# Revit family: RN 55033 Optipress-Therm-Übergang
name_source: partatom
category: Rohrformteile
units: mm (PartAtom-declared; Revit-internal decimal feet)

## family parameters
Arbeitsebenenbasiert = Nein
Beim Laden mit Abzugskörper schneiden = Nein
Bemaßung runder Anschluss = Durchmesser verwenden
Gemeinsam genutzt = Nein
Immer vertikal = Ja
Teiletyp = Verbindung

## types (22) — shared parameters
1.010.00.2 Blattnummer der Richtlinie = 29
1.010.00.3 Ausgabedatum (Monat) der Richtlinie = 201308
1.010.00.4 Herstellername = R. Nussbaum AG
1.010.00.5 Revisionsdatum der Datei = 20190521
1.010.00.6 Webadresse des Herstellers = http://www.nussbaum.ch
1.100.00.4 Produktbezeichnung = Versorgung
1.110.00.2 Index = 1
1.110.00.4 Produktbezeichnung = Optipress-Therm
1.960/3L.00.8 Link (URL) = https://www.nussbaum.ch
29.700.00.4 Produktname = Optipress-Therm-Übergang, mit Innengewinde
29.700.00.5 Produktkennung = 2
29.700.00.6 Querschnittsform = 1
29.700.00.7 Nennweitensystem = DN
29.700.00.8 Nenndrucksystem = PN
29.710.02.4 Nenndruck = 16
29.710.02.5 max. zul. Überdruck [hPa] = 1600
29.710.02.7 max. zul. Dauer-Betriebsdruck [hPa] = 1600
29.710.02.9 max. zul. Dauer-Betriebstemperatur [°C] = 95
Connector Visibility = Nein
EnclosingSpace Visibility = Nein

## per-type parameters (varying)
- DN=60x50: 1.800.00.3 TGA-Nummer=01900100000000000000000000000000000000000000000020000000000000000022; 1.800.00.4 Kommentarfeld=55033.70, Optipress-Therm-Übergang, mit Innengewinde, DN=60x50, L=88, Rp=2; 1.810.00.3 Hersteller-Bestellnummer=55033.7; 1.810.00.4 DATANORM-Nummer=55033.70; 1.810.00.5 StLB-Nummer=255.644; 1.810.00.6 GTIN-Nummer=7612945685605; 29.710.02.10 Formstück-Gewicht [kg]=0.403; 29.710.02.3 Benennung=Optipress-Therm-Übergang, mit Innengewinde, DN=60x50, L=88, Rp=2; CONNECTOR0_DIAMETER_dX_0r=60 mm; CONNECTOR0_dX_01=43 mm  [stored 0.141076 ft]; CONNECTOR0_ref_dX=43 mm  [stored 0.141076 ft]; CONNECTOR1_DIAMETER_dX_0r=50 mm; CONNECTOR1_dX_00=89 mm; CONNECTOR1_dX_01=113 mm; CONNECTOR1_ref_dX=113 mm; Hersteller=R. Nussbaum AG; Modell=55033.7; R. Nussbaum AG 55033.21 de Visibility=Nein; R. Nussbaum AG 55033.22 de Visibility=Nein; R. Nussbaum AG 55033.23 de Visibility=Nein; R. Nussbaum AG 55033.24 de Visibility=Nein; R. Nussbaum AG 55033.25 de Visibility=Nein; R. Nussbaum AG 55033.26 de Visibility=Nein; R. Nussbaum AG 55033.27 de Visibility=Nein; R. Nussbaum AG 55033.28 de Visibility=Nein; R. Nussbaum AG 55033.29 de Visibility=Nein; R. Nussbaum AG 55033.30 de Visibility=Nein; R. Nussbaum AG 55033.31 de Visibility=Nein; R. Nussbaum AG 55033.32 de Visibility=Nein; R. Nussbaum AG 55033.33 de Visibility=Nein; R. Nussbaum AG 55033.34 de Visibility=Nein; R. Nussbaum AG 55033.35 de Visibility=Nein; R. Nussbaum AG 55033.36 de Visibility=Nein; R. Nussbaum AG 55033.37 de Visibility=Nein; R. Nussbaum AG 55033.70 de Visibility=Ja; R. Nussbaum AG 55033.71 de Visibility=Nein; R. Nussbaum AG 55033.72 de Visibility=Nein; R. Nussbaum AG 55033.73 de Visibility=Nein; R. Nussbaum AG 55033.74 de Visibility=Nein; Typenkommentare=Optipress-Therm-Übergang DN=60x50
- DN=25x15: 1.800.00.3 TGA-Nummer=01900100000000000000000000000000000000000000000020000000000000000021; 1.800.00.4 Kommentarfeld=55033.30, Optipress-Therm-Übergang, mit Innengewinde, DN=25x15, L=38, Rp=½; 1.810.00.3 Hersteller-Bestellnummer=55033.3; 1.810.00.4 DATANORM-Nummer=55033.30; 1.810.00.5 StLB-Nummer=255.635; 1.810.00.6 GTIN-Nummer=7612945708946; 29.710.02.10 Formstück-Gewicht [kg]=0.115; 29.710.02.3 Benennung=Optipress-Therm-Übergang, mit Innengewinde, DN=25x15, L=38, Rp=½; CONNECTOR0_DIAMETER_dX_0r=25 mm  [stored 0.082021 ft]; CONNECTOR0_dX_01=24 mm; CONNECTOR0_ref_dX=24 mm; CONNECTOR1_DIAMETER_dX_0r=15 mm  [stored 0.0492126 ft]; CONNECTOR1_dX_00=24 mm; CONNECTOR1_dX_01=38 mm  [stored 0.124672 ft]; CONNECTOR1_ref_dX=24 mm; Hersteller=R. Nussbaum AG; Modell=55033.3; R. Nussbaum AG 55033.21 de Visibility=Nein; R. Nussbaum AG 55033.22 de Visibility=Nein; R. Nussbaum AG 55033.23 de Visibility=Nein; R. Nussbaum AG 55033.24 de Visibility=Nein; R. Nussbaum AG 55033.25 de Visibility=Nein; R. Nussbaum AG 55033.26 de Visibility=Nein; R. Nussbaum AG 55033.27 de Visibility=Nein; R. Nussbaum AG 55033.28 de Visibility=Nein; R. Nussbaum AG 55033.29 de Visibility=Nein; R. Nussbaum AG 55033.30 de Visibility=Ja; R. Nussbaum AG 55033.31 de Visibility=Nein; R. Nussbaum AG 55033.32 de Visibility=Nein; R. Nussbaum AG 55033.33 de Visibility=Nein; R. Nussbaum AG 55033.34 de Visibility=Nein; R. Nussbaum AG 55033.35 de Visibility=Nein; R. Nussbaum AG 55033.36 de Visibility=Nein; R. Nussbaum AG 55033.37 de Visibility=Nein; R. Nussbaum AG 55033.70 de Visibility=Nein; R. Nussbaum AG 55033.71 de Visibility=Nein; R. Nussbaum AG 55033.72 de Visibility=Nein; R. Nussbaum AG 55033.73 de Visibility=Nein; R. Nussbaum AG 55033.74 de Visibility=Nein; Typenkommentare=Optipress-Therm-Übergang DN=25x15
- DN=100: 1.800.00.3 TGA-Nummer=01900100000000000000000000000000000000000000000020000000000000000020; 1.800.00.4 Kommentarfeld=55033.74, Optipress-Therm-Übergang, mit Innengewinde, DN=100, L=135, Rp=4; 1.810.00.3 Hersteller-Bestellnummer=55033.74; 1.810.00.4 DATANORM-Nummer=55033.74; 1.810.00.5 StLB-Nummer=255.643; 1.810.00.6 GTIN-Nummer=7612945699220; 29.710.02.10 Formstück-Gewicht [kg]=1.453; 29.710.02.3 Benennung=Optipress-Therm-Übergang, mit Innengewinde, DN=100, L=135, Rp=4; CONNECTOR0_DIAMETER_dX_0r=100 mm  [stored 0.328084 ft]; CONNECTOR0_dX_01=60 mm; CONNECTOR0_ref_dX=60 mm; CONNECTOR1_DIAMETER_dX_0r=100 mm  [stored 0.328084 ft]; CONNECTOR1_dX_00=98 mm; CONNECTOR1_dX_01=134 mm; CONNECTOR1_ref_dX=98 mm; Hersteller=R. Nussbaum AG; Modell=55033.74; R. Nussbaum AG 55033.21 de Visibility=Nein; R. Nussbaum AG 55033.22 de Visibility=Nein; R. Nussbaum AG 55033.23 de Visibility=Nein; R. Nussbaum AG 55033.24 de Visibility=Nein; R. Nussbaum AG 55033.25 de Visibility=Nein; R. Nussbaum AG 55033.26 de Visibility=Nein; R. Nussbaum AG 55033.27 de Visibility=Nein; R. Nussbaum AG 55033.28 de Visibility=Nein; R. Nussbaum AG 55033.29 de Visibility=Nein; R. Nussbaum AG 55033.30 de Visibility=Nein; R. Nussbaum AG 55033.31 de Visibility=Nein; R. Nussbaum AG 55033.32 de Visibility=Nein; R. Nussbaum AG 55033.33 de Visibility=Nein; R. Nussbaum AG 55033.34 de Visibility=Nein; R. Nussbaum AG 55033.35 de Visibility=Nein; R. Nussbaum AG 55033.36 de Visibility=Nein; R. Nussbaum AG 55033.37 de Visibility=Nein; R. Nussbaum AG 55033.70 de Visibility=Nein; R. Nussbaum AG 55033.71 de Visibility=Nein; R. Nussbaum AG 55033.72 de Visibility=Nein; R. Nussbaum AG 55033.73 de Visibility=Nein; R. Nussbaum AG 55033.74 de Visibility=Ja; Typenkommentare=Optipress-Therm-Übergang DN=100
- DN=80: 1.800.00.3 TGA-Nummer=01900100000000000000000000000000000000000000000020000000000000000019; 1.800.00.4 Kommentarfeld=55033.73, Optipress-Therm-Übergang, mit Innengewinde, DN=80, L=114, Rp=3; 1.810.00.3 Hersteller-Bestellnummer=55033.73; 1.810.00.4 DATANORM-Nummer=55033.73; 1.810.00.5 StLB-Nummer=255.642; 1.810.00.6 GTIN-Nummer=7612945699213; 29.710.02.10 Formstück-Gewicht [kg]=1.165; 29.710.02.3 Benennung=Optipress-Therm-Übergang, mit Innengewinde, DN=80, L=114, Rp=3; CONNECTOR0_DIAMETER_dX_0r=80 mm; CONNECTOR0_dX_01=50 mm; CONNECTOR0_ref_dX=50 mm; CONNECTOR1_DIAMETER_dX_0r=80 mm; CONNECTOR1_dX_00=84 mm; CONNECTOR1_dX_01=114 mm; CONNECTOR1_ref_dX=84 mm; Hersteller=R. Nussbaum AG; Modell=55033.73; R. Nussbaum AG 55033.21 de Visibility=Nein; R. Nussbaum AG 55033.22 de Visibility=Nein; R. Nussbaum AG 55033.23 de Visibility=Nein; R. Nussbaum AG 55033.24 de Visibility=Nein; R. Nussbaum AG 55033.25 de Visibility=Nein; R. Nussbaum AG 55033.26 de Visibility=Nein; R. Nussbaum AG 55033.27 de Visibility=Nein; R. Nussbaum AG 55033.28 de Visibility=Nein; R. Nussbaum AG 55033.29 de Visibility=Nein; R. Nussbaum AG 55033.30 de Visibility=Nein; R. Nussbaum AG 55033.31 de Visibility=Nein; R. Nussbaum AG 55033.32 de Visibility=Nein; R. Nussbaum AG 55033.33 de Visibility=Nein; R. Nussbaum AG 55033.34 de Visibility=Nein; R. Nussbaum AG 55033.35 de Visibility=Nein; R. Nussbaum AG 55033.36 de Visibility=Nein; R. Nussbaum AG 55033.37 de Visibility=Nein; R. Nussbaum AG 55033.70 de Visibility=Nein; R. Nussbaum AG 55033.71 de Visibility=Nein; R. Nussbaum AG 55033.72 de Visibility=Nein; R. Nussbaum AG 55033.73 de Visibility=Ja; R. Nussbaum AG 55033.74 de Visibility=Nein; Typenkommentare=Optipress-Therm-Übergang DN=80
- DN=65: 1.800.00.3 TGA-Nummer=01900100000000000000000000000000000000000000000020000000000000000018; 1.800.00.4 Kommentarfeld=55033.72, Optipress-Therm-Übergang, mit Innengewinde, DN=65, L=104, Rp=2½; 1.810.00.3 Hersteller-Bestellnummer=55033.72; 1.810.00.4 DATANORM-Nummer=55033.72; 1.810.00.5 StLB-Nummer=255.641; 1.810.00.6 GTIN-Nummer=7612945685629; 29.710.02.10 Formstück-Gewicht [kg]=0.67; 29.710.02.3 Benennung=Optipress-Therm-Übergang, mit Innengewinde, DN=65, L=104, Rp=2½; CONNECTOR0_DIAMETER_dX_0r=65 mm; CONNECTOR0_dX_01=50 mm; CONNECTOR0_ref_dX=50 mm; CONNECTOR1_DIAMETER_dX_0r=65 mm; CONNECTOR1_dX_00=78 mm; CONNECTOR1_dX_01=105 mm; CONNECTOR1_ref_dX=78 mm; Hersteller=R. Nussbaum AG; Modell=55033.72; R. Nussbaum AG 55033.21 de Visibility=Nein; R. Nussbaum AG 55033.22 de Visibility=Nein; R. Nussbaum AG 55033.23 de Visibility=Nein; R. Nussbaum AG 55033.24 de Visibility=Nein; R. Nussbaum AG 55033.25 de Visibility=Nein; R. Nussbaum AG 55033.26 de Visibility=Nein; R. Nussbaum AG 55033.27 de Visibility=Nein; R. Nussbaum AG 55033.28 de Visibility=Nein; R. Nussbaum AG 55033.29 de Visibility=Nein; R. Nussbaum AG 55033.30 de Visibility=Nein; R. Nussbaum AG 55033.31 de Visibility=Nein; R. Nussbaum AG 55033.32 de Visibility=Nein; R. Nussbaum AG 55033.33 de Visibility=Nein; R. Nussbaum AG 55033.34 de Visibility=Nein; R. Nussbaum AG 55033.35 de Visibility=Nein; R. Nussbaum AG 55033.36 de Visibility=Nein; R. Nussbaum AG 55033.37 de Visibility=Nein; R. Nussbaum AG 55033.70 de Visibility=Nein; R. Nussbaum AG 55033.71 de Visibility=Nein; R. Nussbaum AG 55033.72 de Visibility=Ja; R. Nussbaum AG 55033.73 de Visibility=Nein; R. Nussbaum AG 55033.74 de Visibility=Nein; Typenkommentare=Optipress-Therm-Übergang DN=65
- DN=60x65: 1.800.00.3 TGA-Nummer=01900100000000000000000000000000000000000000000020000000000000000017; 1.800.00.4 Kommentarfeld=55033.71, Optipress-Therm-Übergang, mit Innengewinde, DN=60x65, L=98, Rp=2½; 1.810.00.3 Hersteller-Bestellnummer=55033.71; 1.810.00.4 DATANORM-Nummer=55033.71; 1.810.00.5 StLB-Nummer=255.644; 1.810.00.6 GTIN-Nummer=7612945685612; 29.710.02.10 Formstück-Gewicht [kg]=0.649; 29.710.02.3 Benennung=Optipress-Therm-Übergang, mit Innengewinde, DN=60x65, L=98, Rp=2½; CONNECTOR0_DIAMETER_dX_0r=60 mm; CONNECTOR0_dX_01=43 mm  [stored 0.141076 ft]; CONNECTOR0_ref_dX=43 mm  [stored 0.141076 ft]; CONNECTOR1_DIAMETER_dX_0r=50 mm; CONNECTOR1_dX_00=99 mm; CONNECTOR1_dX_01=126 mm; CONNECTOR1_ref_dX=126 mm; Hersteller=R. Nussbaum AG; Modell=55033.71; R. Nussbaum AG 55033.21 de Visibility=Nein; R. Nussbaum AG 55033.22 de Visibility=Nein; R. Nussbaum AG 55033.23 de Visibility=Nein; R. Nussbaum AG 55033.24 de Visibility=Nein; R. Nussbaum AG 55033.25 de Visibility=Nein; R. Nussbaum AG 55033.26 de Visibility=Nein; R. Nussbaum AG 55033.27 de Visibility=Nein; R. Nussbaum AG 55033.28 de Visibility=Nein; R. Nussbaum AG 55033.29 de Visibility=Nein; R. Nussbaum AG 55033.30 de Visibility=Nein; R. Nussbaum AG 55033.31 de Visibility=Nein; R. Nussbaum AG 55033.32 de Visibility=Nein; R. Nussbaum AG 55033.33 de Visibility=Nein; R. Nussbaum AG 55033.34 de Visibility=Nein; R. Nussbaum AG 55033.35 de Visibility=Nein; R. Nussbaum AG 55033.36 de Visibility=Nein; R. Nussbaum AG 55033.37 de Visibility=Nein; R. Nussbaum AG 55033.70 de Visibility=Nein; R. Nussbaum AG 55033.71 de Visibility=Ja; R. Nussbaum AG 55033.72 de Visibility=Nein; R. Nussbaum AG 55033.73 de Visibility=Nein; R. Nussbaum AG 55033.74 de Visibility=Nein; Typenkommentare=Optipress-Therm-Übergang DN=60x65
- DN=40x32: 1.800.00.3 TGA-Nummer=01900100000000000000000000000000000000000000000020000000000000000016; 1.800.00.4 Kommentarfeld=55033.37, Optipress-Therm-Übergang, mit Innengewinde, DN=40x32, L=63, Rp=1¼; 1.810.00.3 Hersteller-Bestellnummer=55033.37; 1.810.00.4 DATANORM-Nummer=55033.37; 1.810.00.5 StLB-Nummer=255.637; 1.810.00.6 GTIN-Nummer=7612945708960; 29.710.02.10 Formstück-Gewicht [kg]=0.302; 29.710.02.3 Benennung=Optipress-Therm-Übergang, mit Innengewinde, DN=40x32, L=63, Rp=1¼; CONNECTOR0_DIAMETER_dX_0r=40 mm; CONNECTOR0_dX_01=36 mm; CONNECTOR0_ref_dX=36 mm; CONNECTOR1_DIAMETER_dX_0r=32 mm; CONNECTOR1_dX_00=44 mm  [stored 0.144357 ft]; CONNECTOR1_dX_01=63 mm; CONNECTOR1_ref_dX=44 mm  [stored 0.144357 ft]; Hersteller=R. Nussbaum AG; Modell=55033.37; R. Nussbaum AG 55033.21 de Visibility=Nein; R. Nussbaum AG 55033.22 de Visibility=Nein; R. Nussbaum AG 55033.23 de Visibility=Nein; R. Nussbaum AG 55033.24 de Visibility=Nein; R. Nussbaum AG 55033.25 de Visibility=Nein; R. Nussbaum AG 55033.26 de Visibility=Nein; R. Nussbaum AG 55033.27 de Visibility=Nein; R. Nussbaum AG 55033.28 de Visibility=Nein; R. Nussbaum AG 55033.29 de Visibility=Nein; R. Nussbaum AG 55033.30 de Visibility=Nein; R. Nussbaum AG 55033.31 de Visibility=Nein; R. Nussbaum AG 55033.32 de Visibility=Nein; R. Nussbaum AG 55033.33 de Visibility=Nein; R. Nussbaum AG 55033.34 de Visibility=Nein; R. Nussbaum AG 55033.35 de Visibility=Nein; R. Nussbaum AG 55033.36 de Visibility=Nein; R. Nussbaum AG 55033.37 de Visibility=Ja; R. Nussbaum AG 55033.70 de Visibility=Nein; R. Nussbaum AG 55033.71 de Visibility=Nein; R. Nussbaum AG 55033.72 de Visibility=Nein; R. Nussbaum AG 55033.73 de Visibility=Nein; R. Nussbaum AG 55033.74 de Visibility=Nein; Typenkommentare=Optipress-Therm-Übergang DN=40x32
- DN=32x25: 1.800.00.3 TGA-Nummer=01900100000000000000000000000000000000000000000020000000000000000015; 1.800.00.4 Kommentarfeld=55033.36, Optipress-Therm-Übergang, mit Innengewinde, DN=32x25, L=43, Rp=1; 1.810.00.3 Hersteller-Bestellnummer=55033.36; 1.810.00.4 DATANORM-Nummer=55033.36; 1.810.00.5 StLB-Nummer=255.636; 1.810.00.6 GTIN-Nummer=7612945708953; 29.710.02.10 Formstück-Gewicht [kg]=0.155; 29.710.02.3 Benennung=Optipress-Therm-Übergang, mit Innengewinde, DN=32x25, L=43, Rp=1; CONNECTOR0_DIAMETER_dX_0r=32 mm; CONNECTOR0_dX_01=26 mm; CONNECTOR0_ref_dX=26 mm; CONNECTOR1_DIAMETER_dX_0r=25 mm  [stored 0.082021 ft]; CONNECTOR1_dX_00=26 mm; CONNECTOR1_dX_01=43 mm  [stored 0.141076 ft]; CONNECTOR1_ref_dX=26 mm; Hersteller=R. Nussbaum AG; Modell=55033.36; R. Nussbaum AG 55033.21 de Visibility=Nein; R. Nussbaum AG 55033.22 de Visibility=Nein; R. Nussbaum AG 55033.23 de Visibility=Nein; R. Nussbaum AG 55033.24 de Visibility=Nein; R. Nussbaum AG 55033.25 de Visibility=Nein; R. Nussbaum AG 55033.26 de Visibility=Nein; R. Nussbaum AG 55033.27 de Visibility=Nein; R. Nussbaum AG 55033.28 de Visibility=Nein; R. Nussbaum AG 55033.29 de Visibility=Nein; R. Nussbaum AG 55033.30 de Visibility=Nein; R. Nussbaum AG 55033.31 de Visibility=Nein; R. Nussbaum AG 55033.32 de Visibility=Nein; R. Nussbaum AG 55033.33 de Visibility=Nein; R. Nussbaum AG 55033.34 de Visibility=Nein; R. Nussbaum AG 55033.35 de Visibility=Nein; R. Nussbaum AG 55033.36 de Visibility=Ja; R. Nussbaum AG 55033.37 de Visibility=Nein; R. Nussbaum AG 55033.70 de Visibility=Nein; R. Nussbaum AG 55033.71 de Visibility=Nein; R. Nussbaum AG 55033.72 de Visibility=Nein; R. Nussbaum AG 55033.73 de Visibility=Nein; R. Nussbaum AG 55033.74 de Visibility=Nein; Typenkommentare=Optipress-Therm-Übergang DN=32x25
- DN=50: 1.800.00.3 TGA-Nummer=01900100000000000000000000000000000000000000000020000000000000000014; 1.800.00.4 Kommentarfeld=55033.35, Optipress-Therm-Übergang, mit Innengewinde, DN=50, L=72, Rp=2; 1.810.00.3 Hersteller-Bestellnummer=55033.35; 1.810.00.4 DATANORM-Nummer=55033.35; 1.810.00.5 StLB-Nummer=255.638; 1.810.00.6 GTIN-Nummer=7612945685599; 29.710.02.10 Formstück-Gewicht [kg]=0.422; 29.710.02.3 Benennung=Optipress-Therm-Übergang, mit Innengewinde, DN=50, L=72, Rp=2; CONNECTOR0_DIAMETER_dX_0r=50 mm; CONNECTOR0_dX_01=40 mm; CONNECTOR0_ref_dX=40 mm; CONNECTOR1_DIAMETER_dX_0r=50 mm; CONNECTOR1_dX_00=48 mm  [stored 0.15748 ft]; CONNECTOR1_dX_01=72 mm; CONNECTOR1_ref_dX=48 mm  [stored 0.15748 ft]; R. Nussbaum AG 55033.21 de Visibility=Nein; R. Nussbaum AG 55033.22 de Visibility=Nein; R. Nussbaum AG 55033.23 de Visibility=Nein; R. Nussbaum AG 55033.24 de Visibility=Nein; R. Nussbaum AG 55033.25 de Visibility=Nein; R. Nussbaum AG 55033.26 de Visibility=Nein; R. Nussbaum AG 55033.27 de Visibility=Nein; R. Nussbaum AG 55033.28 de Visibility=Nein; R. Nussbaum AG 55033.29 de Visibility=Nein; R. Nussbaum AG 55033.30 de Visibility=Nein; R. Nussbaum AG 55033.31 de Visibility=Nein; R. Nussbaum AG 55033.32 de Visibility=Nein; R. Nussbaum AG 55033.33 de Visibility=Nein; R. Nussbaum AG 55033.34 de Visibility=Nein; R. Nussbaum AG 55033.35 de Visibility=Ja; R. Nussbaum AG 55033.36 de Visibility=Nein; R. Nussbaum AG 55033.37 de Visibility=Nein; R. Nussbaum AG 55033.70 de Visibility=Nein; R. Nussbaum AG 55033.71 de Visibility=Nein; R. Nussbaum AG 55033.72 de Visibility=Nein; R. Nussbaum AG 55033.73 de Visibility=Nein; R. Nussbaum AG 55033.74 de Visibility=Nein
- DN=40: 1.800.00.3 TGA-Nummer=01900100000000000000000000000000000000000000000020000000000000000013; 1.800.00.4 Kommentarfeld=55033.34, Optipress-Therm-Übergang, mit Innengewinde, DN=40, L=63, Rp=1½; 1.810.00.3 Hersteller-Bestellnummer=55033.34; 1.810.00.4 DATANORM-Nummer=55033.34; 1.810.00.5 StLB-Nummer=255.637; 1.810.00.6 GTIN-Nummer=7612945685582; 29.710.02.10 Formstück-Gewicht [kg]=0.237; 29.710.02.3 Benennung=Optipress-Therm-Übergang, mit Innengewinde, DN=40, L=63, Rp=1½; CONNECTOR0_DIAMETER_dX_0r=40 mm; CONNECTOR0_dX_01=36 mm; CONNECTOR0_ref_dX=36 mm; CONNECTOR1_DIAMETER_dX_0r=40 mm; CONNECTOR1_dX_00=44 mm  [stored 0.144357 ft]; CONNECTOR1_dX_01=63 mm; CONNECTOR1_ref_dX=44 mm  [stored 0.144357 ft]; R. Nussbaum AG 55033.21 de Visibility=Nein; R. Nussbaum AG 55033.22 de Visibility=Nein; R. Nussbaum AG 55033.23 de Visibility=Nein; R. Nussbaum AG 55033.24 de Visibility=Nein; R. Nussbaum AG 55033.25 de Visibility=Nein; R. Nussbaum AG 55033.26 de Visibility=Nein; R. Nussbaum AG 55033.27 de Visibility=Nein; R. Nussbaum AG 55033.28 de Visibility=Nein; R. Nussbaum AG 55033.29 de Visibility=Nein; R. Nussbaum AG 55033.30 de Visibility=Nein; R. Nussbaum AG 55033.31 de Visibility=Nein; R. Nussbaum AG 55033.32 de Visibility=Nein; R. Nussbaum AG 55033.33 de Visibility=Nein; R. Nussbaum AG 55033.34 de Visibility=Ja; R. Nussbaum AG 55033.35 de Visibility=Nein; R. Nussbaum AG 55033.36 de Visibility=Nein; R. Nussbaum AG 55033.37 de Visibility=Nein; R. Nussbaum AG 55033.70 de Visibility=Nein; R. Nussbaum AG 55033.71 de Visibility=Nein; R. Nussbaum AG 55033.72 de Visibility=Nein; R. Nussbaum AG 55033.73 de Visibility=Nein; R. Nussbaum AG 55033.74 de Visibility=Nein
- DN=32: 1.800.00.3 TGA-Nummer=01900100000000000000000000000000000000000000000020000000000000000012; 1.800.00.4 Kommentarfeld=55033.33, Optipress-Therm-Übergang, mit Innengewinde, DN=32, L=52, Rp=1¼; 1.810.00.3 Hersteller-Bestellnummer=55033.33; 1.810.00.4 DATANORM-Nummer=55033.33; 1.810.00.5 StLB-Nummer=255.636; 1.810.00.6 GTIN-Nummer=7612945685575; 29.710.02.10 Formstück-Gewicht [kg]=0.167; 29.710.02.3 Benennung=Optipress-Therm-Übergang, mit Innengewinde, DN=32, L=52, Rp=1¼; CONNECTOR0_DIAMETER_dX_0r=32 mm; CONNECTOR0_dX_01=26 mm; CONNECTOR0_ref_dX=26 mm; CONNECTOR1_DIAMETER_dX_0r=32 mm; CONNECTOR1_dX_00=34 mm; CONNECTOR1_dX_01=53 mm; CONNECTOR1_ref_dX=34 mm; R. Nussbaum AG 55033.21 de Visibility=Nein; R. Nussbaum AG 55033.22 de Visibility=Nein; R. Nussbaum AG 55033.23 de Visibility=Nein; R. Nussbaum AG 55033.24 de Visibility=Nein; R. Nussbaum AG 55033.25 de Visibility=Nein; R. Nussbaum AG 55033.26 de Visibility=Nein; R. Nussbaum AG 55033.27 de Visibility=Nein; R. Nussbaum AG 55033.28 de Visibility=Nein; R. Nussbaum AG 55033.29 de Visibility=Nein; R. Nussbaum AG 55033.30 de Visibility=Nein; R. Nussbaum AG 55033.31 de Visibility=Nein; R. Nussbaum AG 55033.32 de Visibility=Nein; R. Nussbaum AG 55033.33 de Visibility=Ja; R. Nussbaum AG 55033.34 de Visibility=Nein; R. Nussbaum AG 55033.35 de Visibility=Nein; R. Nussbaum AG 55033.36 de Visibility=Nein; R. Nussbaum AG 55033.37 de Visibility=Nein; R. Nussbaum AG 55033.70 de Visibility=Nein; R. Nussbaum AG 55033.71 de Visibility=Nein; R. Nussbaum AG 55033.72 de Visibility=Nein; R. Nussbaum AG 55033.73 de Visibility=Nein; R. Nussbaum AG 55033.74 de Visibility=Nein
- DN=32x20: 1.800.00.3 TGA-Nummer=01900100000000000000000000000000000000000000000020000000000000000011; 1.800.00.4 Kommentarfeld=55033.32, Optipress-Therm-Übergang, mit Innengewinde, DN=32x20, L=43, Rp=¾; 1.810.00.3 Hersteller-Bestellnummer=55033.32; 1.810.00.4 DATANORM-Nummer=55033.32; 1.810.00.5 StLB-Nummer=255.636; 1.810.00.6 GTIN-Nummer=7612945685568; 29.710.02.10 Formstück-Gewicht [kg]=0.19; 29.710.02.3 Benennung=Optipress-Therm-Übergang, mit Innengewinde, DN=32x20, L=43, Rp=¾; CONNECTOR0_DIAMETER_dX_0r=32 mm; CONNECTOR0_dX_01=26 mm; CONNECTOR0_ref_dX=26 mm; CONNECTOR1_DIAMETER_dX_0r=20 mm; CONNECTOR1_dX_00=28 mm; CONNECTOR1_dX_01=43 mm  [stored 0.141076 ft]; CONNECTOR1_ref_dX=28 mm; R. Nussbaum AG 55033.21 de Visibility=Nein; R. Nussbaum AG 55033.22 de Visibility=Nein; R. Nussbaum AG 55033.23 de Visibility=Nein; R. Nussbaum AG 55033.24 de Visibility=Nein; R. Nussbaum AG 55033.25 de Visibility=Nein; R. Nussbaum AG 55033.26 de Visibility=Nein; R. Nussbaum AG 55033.27 de Visibility=Nein; R. Nussbaum AG 55033.28 de Visibility=Nein; R. Nussbaum AG 55033.29 de Visibility=Nein; R. Nussbaum AG 55033.30 de Visibility=Nein; R. Nussbaum AG 55033.31 de Visibility=Nein; R. Nussbaum AG 55033.32 de Visibility=Ja; R. Nussbaum AG 55033.33 de Visibility=Nein; R. Nussbaum AG 55033.34 de Visibility=Nein; R. Nussbaum AG 55033.35 de Visibility=Nein; R. Nussbaum AG 55033.36 de Visibility=Nein; R. Nussbaum AG 55033.37 de Visibility=Nein; R. Nussbaum AG 55033.70 de Visibility=Nein; R. Nussbaum AG 55033.71 de Visibility=Nein; R. Nussbaum AG 55033.72 de Visibility=Nein; R. Nussbaum AG 55033.73 de Visibility=Nein; R. Nussbaum AG 55033.74 de Visibility=Nein
- DN=25x20: 1.800.00.3 TGA-Nummer=01900100000000000000000000000000000000000000000020000000000000000010; 1.800.00.4 Kommentarfeld=55033.31, Optipress-Therm-Übergang, mit Innengewinde, DN=25x20, L=44, Rp=¾; 1.810.00.3 Hersteller-Bestellnummer=55033.31; 1.810.00.4 DATANORM-Nummer=55033.31; 1.810.00.5 StLB-Nummer=255.635; 1.810.00.6 GTIN-Nummer=7612945685551; 29.710.02.10 Formstück-Gewicht [kg]=0.099; 29.710.02.3 Benennung=Optipress-Therm-Übergang, mit Innengewinde, DN=25x20, L=44, Rp=¾; CONNECTOR0_DIAMETER_dX_0r=25 mm  [stored 0.082021 ft]; CONNECTOR0_dX_01=24 mm; CONNECTOR0_ref_dX=24 mm; CONNECTOR1_DIAMETER_dX_0r=20 mm; CONNECTOR1_dX_00=27 mm; CONNECTOR1_dX_01=44 mm  [stored 0.144357 ft]; CONNECTOR1_ref_dX=27 mm; R. Nussbaum AG 55033.21 de Visibility=Nein; R. Nussbaum AG 55033.22 de Visibility=Nein; R. Nussbaum AG 55033.23 de Visibility=Nein; R. Nussbaum AG 55033.24 de Visibility=Nein; R. Nussbaum AG 55033.25 de Visibility=Nein; R. Nussbaum AG 55033.26 de Visibility=Nein; R. Nussbaum AG 55033.27 de Visibility=Nein; R. Nussbaum AG 55033.28 de Visibility=Nein; R. Nussbaum AG 55033.29 de Visibility=Nein; R. Nussbaum AG 55033.30 de Visibility=Nein; R. Nussbaum AG 55033.31 de Visibility=Ja; R. Nussbaum AG 55033.32 de Visibility=Nein; R. Nussbaum AG 55033.33 de Visibility=Nein; R. Nussbaum AG 55033.34 de Visibility=Nein; R. Nussbaum AG 55033.35 de Visibility=Nein; R. Nussbaum AG 55033.36 de Visibility=Nein; R. Nussbaum AG 55033.37 de Visibility=Nein; R. Nussbaum AG 55033.70 de Visibility=Nein; R. Nussbaum AG 55033.71 de Visibility=Nein; R. Nussbaum AG 55033.72 de Visibility=Nein; R. Nussbaum AG 55033.73 de Visibility=Nein; R. Nussbaum AG 55033.74 de Visibility=Nein
- DN=20x25: 1.800.00.3 TGA-Nummer=01900100000000000000000000000000000000000000000020000000000000000009; 1.800.00.4 Kommentarfeld=55033.29, Optipress-Therm-Übergang, mit Innengewinde, DN=20x25, L=48, Rp=1; 1.810.00.3 Hersteller-Bestellnummer=55033.29; 1.810.00.4 DATANORM-Nummer=55033.29; 1.810.00.5 StLB-Nummer=255.634; 1.810.00.6 GTIN-Nummer=7612945685544; 29.710.02.10 Formstück-Gewicht [kg]=0.086; 29.710.02.3 Benennung=Optipress-Therm-Übergang, mit Innengewinde, DN=20x25, L=48, Rp=1; CONNECTOR0_DIAMETER_dX_0r=20 mm; CONNECTOR0_dX_01=24 mm; CONNECTOR0_ref_dX=24 mm; CONNECTOR1_DIAMETER_dX_0r=25 mm  [stored 0.082021 ft]; CONNECTOR1_dX_00=31 mm; CONNECTOR1_dX_01=48 mm  [stored 0.15748 ft]; CONNECTOR1_ref_dX=31 mm; R. Nussbaum AG 55033.21 de Visibility=Nein; R. Nussbaum AG 55033.22 de Visibility=Nein; R. Nussbaum AG 55033.23 de Visibility=Nein; R. Nussbaum AG 55033.24 de Visibility=Nein; R. Nussbaum AG 55033.25 de Visibility=Nein; R. Nussbaum AG 55033.26 de Visibility=Nein; R. Nussbaum AG 55033.27 de Visibility=Nein; R. Nussbaum AG 55033.28 de Visibility=Nein; R. Nussbaum AG 55033.29 de Visibility=Ja; R. Nussbaum AG 55033.30 de Visibility=Nein; R. Nussbaum AG 55033.31 de Visibility=Nein; R. Nussbaum AG 55033.32 de Visibility=Nein; R. Nussbaum AG 55033.33 de Visibility=Nein; R. Nussbaum AG 55033.34 de Visibility=Nein; R. Nussbaum AG 55033.35 de Visibility=Nein; R. Nussbaum AG 55033.36 de Visibility=Nein; R. Nussbaum AG 55033.37 de Visibility=Nein; R. Nussbaum AG 55033.70 de Visibility=Nein; R. Nussbaum AG 55033.71 de Visibility=Nein; R. Nussbaum AG 55033.72 de Visibility=Nein; R. Nussbaum AG 55033.73 de Visibility=Nein; R. Nussbaum AG 55033.74 de Visibility=Nein
- DN=20x15: 1.800.00.3 TGA-Nummer=01900100000000000000000000000000000000000000000020000000000000000008; 1.800.00.4 Kommentarfeld=55033.28, Optipress-Therm-Übergang, mit Innengewinde, DN=20x15, L=41, Rp=½; 1.810.00.3 Hersteller-Bestellnummer=55033.28; 1.810.00.4 DATANORM-Nummer=55033.28; 1.810.00.5 StLB-Nummer=255.634; 1.810.00.6 GTIN-Nummer=7612945685537; 29.710.02.10 Formstück-Gewicht [kg]=0.065; 29.710.02.3 Benennung=Optipress-Therm-Übergang, mit Innengewinde, DN=20x15, L=41, Rp=½; CONNECTOR0_DIAMETER_dX_0r=20 mm; CONNECTOR0_dX_01=24 mm; CONNECTOR0_ref_dX=24 mm; CONNECTOR1_DIAMETER_dX_0r=15 mm  [stored 0.0492126 ft]; CONNECTOR1_dX_00=28 mm; CONNECTOR1_dX_01=41 mm  [stored 0.134514 ft]; CONNECTOR1_ref_dX=28 mm; R. Nussbaum AG 55033.21 de Visibility=Nein; R. Nussbaum AG 55033.22 de Visibility=Nein; R. Nussbaum AG 55033.23 de Visibility=Nein; R. Nussbaum AG 55033.24 de Visibility=Nein; R. Nussbaum AG 55033.25 de Visibility=Nein; R. Nussbaum AG 55033.26 de Visibility=Nein; R. Nussbaum AG 55033.27 de Visibility=Nein; R. Nussbaum AG 55033.28 de Visibility=Ja; R. Nussbaum AG 55033.29 de Visibility=Nein; R. Nussbaum AG 55033.30 de Visibility=Nein; R. Nussbaum AG 55033.31 de Visibility=Nein; R. Nussbaum AG 55033.32 de Visibility=Nein; R. Nussbaum AG 55033.33 de Visibility=Nein; R. Nussbaum AG 55033.34 de Visibility=Nein; R. Nussbaum AG 55033.35 de Visibility=Nein; R. Nussbaum AG 55033.36 de Visibility=Nein; R. Nussbaum AG 55033.37 de Visibility=Nein; R. Nussbaum AG 55033.70 de Visibility=Nein; R. Nussbaum AG 55033.71 de Visibility=Nein; R. Nussbaum AG 55033.72 de Visibility=Nein; R. Nussbaum AG 55033.73 de Visibility=Nein; R. Nussbaum AG 55033.74 de Visibility=Nein
- DN=15x20: 1.800.00.3 TGA-Nummer=01900100000000000000000000000000000000000000000020000000000000000007; 1.800.00.4 Kommentarfeld=55033.27, Optipress-Therm-Übergang, mit Innengewinde, DN=15x20, L=45, Rp=¾; 1.810.00.3 Hersteller-Bestellnummer=55033.27; 1.810.00.4 DATANORM-Nummer=55033.27; 1.810.00.5 StLB-Nummer=255.632; 1.810.00.6 GTIN-Nummer=7612945685520; 29.710.02.10 Formstück-Gewicht [kg]=0.062; 29.710.02.3 Benennung=Optipress-Therm-Übergang, mit Innengewinde, DN=15x20, L=45, Rp=¾; CONNECTOR0_DIAMETER_dX_0r=15 mm  [stored 0.0492126 ft]; CONNECTOR0_dX_01=22 mm; CONNECTOR0_ref_dX=22 mm; CONNECTOR1_DIAMETER_dX_0r=20 mm; CONNECTOR1_dX_00=30 mm; CONNECTOR1_dX_01=45 mm; CONNECTOR1_ref_dX=30 mm; R. Nussbaum AG 55033.21 de Visibility=Nein; R. Nussbaum AG 55033.22 de Visibility=Nein; R. Nussbaum AG 55033.23 de Visibility=Nein; R. Nussbaum AG 55033.24 de Visibility=Nein; R. Nussbaum AG 55033.25 de Visibility=Nein; R. Nussbaum AG 55033.26 de Visibility=Nein; R. Nussbaum AG 55033.27 de Visibility=Ja; R. Nussbaum AG 55033.28 de Visibility=Nein; R. Nussbaum AG 55033.29 de Visibility=Nein; R. Nussbaum AG 55033.30 de Visibility=Nein; R. Nussbaum AG 55033.31 de Visibility=Nein; R. Nussbaum AG 55033.32 de Visibility=Nein; R. Nussbaum AG 55033.33 de Visibility=Nein; R. Nussbaum AG 55033.34 de Visibility=Nein; R. Nussbaum AG 55033.35 de Visibility=Nein; R. Nussbaum AG 55033.36 de Visibility=Nein; R. Nussbaum AG 55033.37 de Visibility=Nein; R. Nussbaum AG 55033.70 de Visibility=Nein; R. Nussbaum AG 55033.71 de Visibility=Nein; R. Nussbaum AG 55033.72 de Visibility=Nein; R. Nussbaum AG 55033.73 de Visibility=Nein; R. Nussbaum AG 55033.74 de Visibility=Nein
- DN=25: 1.800.00.3 TGA-Nummer=01900100000000000000000000000000000000000000000020000000000000000006; 1.800.00.4 Kommentarfeld=55033.26, Optipress-Therm-Übergang, mit Innengewinde, DN=25, L=48, Rp=1; 1.810.00.3 Hersteller-Bestellnummer=55033.26; 1.810.00.4 DATANORM-Nummer=55033.26; 1.810.00.5 StLB-Nummer=255.635; 1.810.00.6 GTIN-Nummer=7612945662156; 29.710.02.10 Formstück-Gewicht [kg]=0.108; 29.710.02.3 Benennung=Optipress-Therm-Übergang, mit Innengewinde, DN=25, L=48, Rp=1; CONNECTOR0_DIAMETER_dX_0r=25 mm  [stored 0.082021 ft]; CONNECTOR0_dX_01=24 mm; CONNECTOR0_ref_dX=24 mm; CONNECTOR1_DIAMETER_dX_0r=25 mm  [stored 0.082021 ft]; CONNECTOR1_dX_00=31 mm; CONNECTOR1_dX_01=48 mm  [stored 0.15748 ft]; CONNECTOR1_ref_dX=31 mm; Hersteller=R. Nussbaum AG; Modell=55033.26; R. Nussbaum AG 55033.21 de Visibility=Nein; R. Nussbaum AG 55033.22 de Visibility=Nein; R. Nussbaum AG 55033.23 de Visibility=Nein; R. Nussbaum AG 55033.24 de Visibility=Nein; R. Nussbaum AG 55033.25 de Visibility=Nein; R. Nussbaum AG 55033.26 de Visibility=Ja; R. Nussbaum AG 55033.27 de Visibility=Nein; R. Nussbaum AG 55033.28 de Visibility=Nein; R. Nussbaum AG 55033.29 de Visibility=Nein; R. Nussbaum AG 55033.30 de Visibility=Nein; R. Nussbaum AG 55033.31 de Visibility=Nein; R. Nussbaum AG 55033.32 de Visibility=Nein; R. Nussbaum AG 55033.33 de Visibility=Nein; R. Nussbaum AG 55033.34 de Visibility=Nein; R. Nussbaum AG 55033.35 de Visibility=Nein; R. Nussbaum AG 55033.36 de Visibility=Nein; R. Nussbaum AG 55033.37 de Visibility=Nein; R. Nussbaum AG 55033.70 de Visibility=Nein; R. Nussbaum AG 55033.71 de Visibility=Nein; R. Nussbaum AG 55033.72 de Visibility=Nein; R. Nussbaum AG 55033.73 de Visibility=Nein; R. Nussbaum AG 55033.74 de Visibility=Nein; Typenkommentare=Optipress-Therm-Übergang DN=25
- DN=20: 1.800.00.3 TGA-Nummer=01900100000000000000000000000000000000000000000020000000000000000005; 1.800.00.4 Kommentarfeld=55033.25, Optipress-Therm-Übergang, mit Innengewinde, DN=20, L=45, Rp=¾; 1.810.00.3 Hersteller-Bestellnummer=55033.25; 1.810.00.4 DATANORM-Nummer=55033.25; 1.810.00.5 StLB-Nummer=255.634; 1.810.00.6 GTIN-Nummer=7612945662132; 29.710.02.10 Formstück-Gewicht [kg]=0.067; 29.710.02.3 Benennung=Optipress-Therm-Übergang, mit Innengewinde, DN=20, L=45, Rp=¾; CONNECTOR0_DIAMETER_dX_0r=20 mm; CONNECTOR0_dX_01=24 mm; CONNECTOR0_ref_dX=24 mm; CONNECTOR1_DIAMETER_dX_0r=20 mm; CONNECTOR1_dX_00=30 mm; CONNECTOR1_dX_01=45 mm; CONNECTOR1_ref_dX=30 mm; Hersteller=R. Nussbaum AG; Modell=55033.25; R. Nussbaum AG 55033.21 de Visibility=Nein; R. Nussbaum AG 55033.22 de Visibility=Nein; R. Nussbaum AG 55033.23 de Visibility=Nein; R. Nussbaum AG 55033.24 de Visibility=Nein; R. Nussbaum AG 55033.25 de Visibility=Ja; R. Nussbaum AG 55033.26 de Visibility=Nein; R. Nussbaum AG 55033.27 de Visibility=Nein; R. Nussbaum AG 55033.28 de Visibility=Nein; R. Nussbaum AG 55033.29 de Visibility=Nein; R. Nussbaum AG 55033.30 de Visibility=Nein; R. Nussbaum AG 55033.31 de Visibility=Nein; R. Nussbaum AG 55033.32 de Visibility=Nein; R. Nussbaum AG 55033.33 de Visibility=Nein; R. Nussbaum AG 55033.34 de Visibility=Nein; R. Nussbaum AG 55033.35 de Visibility=Nein; R. Nussbaum AG 55033.36 de Visibility=Nein; R. Nussbaum AG 55033.37 de Visibility=Nein; R. Nussbaum AG 55033.70 de Visibility=Nein; R. Nussbaum AG 55033.71 de Visibility=Nein; R. Nussbaum AG 55033.72 de Visibility=Nein; R. Nussbaum AG 55033.73 de Visibility=Nein; R. Nussbaum AG 55033.74 de Visibility=Nein; Typenkommentare=Optipress-Therm-Übergang DN=20
- DN=15x1: 1.800.00.3 TGA-Nummer=01900100000000000000000000000000000000000000000020000000000000000004; 1.800.00.4 Kommentarfeld=55033.24, Optipress-Therm-Übergang, mit Innengewinde, DN=15x20, L=44, Rp=¾; 1.810.00.3 Hersteller-Bestellnummer=55033.24; 1.810.00.4 DATANORM-Nummer=55033.24; 1.810.00.5 StLB-Nummer=255.633; 1.810.00.6 GTIN-Nummer=7612945662538; 29.710.02.10 Formstück-Gewicht [kg]=0.063; 29.710.02.3 Benennung=Optipress-Therm-Übergang, mit Innengewinde, DN=15x20, L=44, Rp=¾; CONNECTOR0_DIAMETER_dX_0r=15 mm  [stored 0.0492126 ft]; CONNECTOR0_dX_01=22 mm; CONNECTOR0_ref_dX=22 mm; CONNECTOR1_DIAMETER_dX_0r=20 mm; CONNECTOR1_dX_00=29 mm; CONNECTOR1_dX_01=44 mm  [stored 0.144357 ft]; CONNECTOR1_ref_dX=29 mm; Hersteller=R. Nussbaum AG; Modell=55033.24; R. Nussbaum AG 55033.21 de Visibility=Nein; R. Nussbaum AG 55033.22 de Visibility=Nein; R. Nussbaum AG 55033.23 de Visibility=Nein; R. Nussbaum AG 55033.24 de Visibility=Ja; R. Nussbaum AG 55033.25 de Visibility=Nein; R. Nussbaum AG 55033.26 de Visibility=Nein; R. Nussbaum AG 55033.27 de Visibility=Nein; R. Nussbaum AG 55033.28 de Visibility=Nein; R. Nussbaum AG 55033.29 de Visibility=Nein; R. Nussbaum AG 55033.30 de Visibility=Nein; R. Nussbaum AG 55033.31 de Visibility=Nein; R. Nussbaum AG 55033.32 de Visibility=Nein; R. Nussbaum AG 55033.33 de Visibility=Nein; R. Nussbaum AG 55033.34 de Visibility=Nein; R. Nussbaum AG 55033.35 de Visibility=Nein; R. Nussbaum AG 55033.36 de Visibility=Nein; R. Nussbaum AG 55033.37 de Visibility=Nein; R. Nussbaum AG 55033.70 de Visibility=Nein; R. Nussbaum AG 55033.71 de Visibility=Nein; R. Nussbaum AG 55033.72 de Visibility=Nein; R. Nussbaum AG 55033.73 de Visibility=Nein; R. Nussbaum AG 55033.74 de Visibility=Nein; Typenkommentare=Optipress-Therm-Übergang DN=15x20
- DN=15: 1.800.00.3 TGA-Nummer=01900100000000000000000000000000000000000000000020000000000000000003; 1.800.00.4 Kommentarfeld=55033.23, Optipress-Therm-Übergang, mit Innengewinde, DN=15, L=41, Rp=½; 1.810.00.3 Hersteller-Bestellnummer=55033.23; 1.810.00.4 DATANORM-Nummer=55033.23; 1.810.00.5 StLB-Nummer=255.633; 1.810.00.6 GTIN-Nummer=7612945662514; 29.710.02.10 Formstück-Gewicht [kg]=0.043; 29.710.02.3 Benennung=Optipress-Therm-Übergang, mit Innengewinde, DN=15, L=41, Rp=½; CONNECTOR0_DIAMETER_dX_0r=15 mm  [stored 0.0492126 ft]; CONNECTOR0_dX_01=22 mm; CONNECTOR0_ref_dX=22 mm; CONNECTOR1_DIAMETER_dX_0r=15 mm  [stored 0.0492126 ft]; CONNECTOR1_dX_00=19 mm; CONNECTOR1_dX_01=41 mm  [stored 0.134514 ft]; CONNECTOR1_ref_dX=19 mm; R. Nussbaum AG 55033.21 de Visibility=Nein; R. Nussbaum AG 55033.22 de Visibility=Nein; R. Nussbaum AG 55033.23 de Visibility=Ja; R. Nussbaum AG 55033.24 de Visibility=Nein; R. Nussbaum AG 55033.25 de Visibility=Nein; R. Nussbaum AG 55033.26 de Visibility=Nein; R. Nussbaum AG 55033.27 de Visibility=Nein; R. Nussbaum AG 55033.28 de Visibility=Nein; R. Nussbaum AG 55033.29 de Visibility=Nein; R. Nussbaum AG 55033.30 de Visibility=Nein; R. Nussbaum AG 55033.31 de Visibility=Nein; R. Nussbaum AG 55033.32 de Visibility=Nein; R. Nussbaum AG 55033.33 de Visibility=Nein; R. Nussbaum AG 55033.34 de Visibility=Nein; R. Nussbaum AG 55033.35 de Visibility=Nein; R. Nussbaum AG 55033.36 de Visibility=Nein; R. Nussbaum AG 55033.37 de Visibility=Nein; R. Nussbaum AG 55033.70 de Visibility=Nein; R. Nussbaum AG 55033.71 de Visibility=Nein; R. Nussbaum AG 55033.72 de Visibility=Nein; R. Nussbaum AG 55033.73 de Visibility=Nein; R. Nussbaum AG 55033.74 de Visibility=Nein
- DN=12x15: 1.800.00.3 TGA-Nummer=01900100000000000000000000000000000000000000000020000000000000000002; 1.800.00.4 Kommentarfeld=55033.22, Optipress-Therm-Übergang, mit Innengewinde, DN=12x15, L=41, Rp=½; 1.810.00.3 Hersteller-Bestellnummer=55033.22; 1.810.00.4 DATANORM-Nummer=55033.22; 1.810.00.5 StLB-Nummer=255.632; 1.810.00.6 GTIN-Nummer=7612945662491; 29.710.02.10 Formstück-Gewicht [kg]=0.038; 29.710.02.3 Benennung=Optipress-Therm-Übergang, mit Innengewinde, DN=12x15, L=41, Rp=½; CONNECTOR0_DIAMETER_dX_0r=12 mm  [stored 0.0393701 ft]; CONNECTOR0_dX_01=22 mm; CONNECTOR0_ref_dX=22 mm; CONNECTOR1_DIAMETER_dX_0r=15 mm  [stored 0.0492126 ft]; CONNECTOR1_dX_00=28 mm; CONNECTOR1_dX_01=41 mm  [stored 0.134514 ft]; CONNECTOR1_ref_dX=28 mm; R. Nussbaum AG 55033.21 de Visibility=Nein; R. Nussbaum AG 55033.22 de Visibility=Ja; R. Nussbaum AG 55033.23 de Visibility=Nein; R. Nussbaum AG 55033.24 de Visibility=Nein; R. Nussbaum AG 55033.25 de Visibility=Nein; R. Nussbaum AG 55033.26 de Visibility=Nein; R. Nussbaum AG 55033.27 de Visibility=Nein; R. Nussbaum AG 55033.28 de Visibility=Nein; R. Nussbaum AG 55033.29 de Visibility=Nein; R. Nussbaum AG 55033.30 de Visibility=Nein; R. Nussbaum AG 55033.31 de Visibility=Nein; R. Nussbaum AG 55033.32 de Visibility=Nein; R. Nussbaum AG 55033.33 de Visibility=Nein; R. Nussbaum AG 55033.34 de Visibility=Nein; R. Nussbaum AG 55033.35 de Visibility=Nein; R. Nussbaum AG 55033.36 de Visibility=Nein; R. Nussbaum AG 55033.37 de Visibility=Nein; R. Nussbaum AG 55033.70 de Visibility=Nein; R. Nussbaum AG 55033.71 de Visibility=Nein; R. Nussbaum AG 55033.72 de Visibility=Nein; R. Nussbaum AG 55033.73 de Visibility=Nein; R. Nussbaum AG 55033.74 de Visibility=Nein
- DN=15x12: 1.800.00.3 TGA-Nummer=01900100000000000000000000000000000000000000000020000000000000000001; 1.800.00.4 Kommentarfeld=55033.21, Optipress-Therm-Übergang, mit Innengewinde, DN=15x12, L=37, Rp=3/8; 1.810.00.3 Hersteller-Bestellnummer=55033.21; 1.810.00.4 DATANORM-Nummer=55033.21; 1.810.00.5 StLB-Nummer=255.632; 1.810.00.6 GTIN-Nummer=7612945685513; 29.710.02.10 Formstück-Gewicht [kg]=0.044; 29.710.02.3 Benennung=Optipress-Therm-Übergang, mit Innengewinde, DN=15x12, L=37, Rp=3/8; CONNECTOR0_DIAMETER_dX_0r=15 mm  [stored 0.0492126 ft]; CONNECTOR0_dX_01=22 mm; CONNECTOR0_ref_dX=22 mm; CONNECTOR1_DIAMETER_dX_0r=12 mm  [stored 0.0393701 ft]; CONNECTOR1_dX_00=27 mm; CONNECTOR1_dX_01=37 mm; CONNECTOR1_ref_dX=27 mm; R. Nussbaum AG 55033.21 de Visibility=Ja; R. Nussbaum AG 55033.22 de Visibility=Nein; R. Nussbaum AG 55033.23 de Visibility=Nein; R. Nussbaum AG 55033.24 de Visibility=Nein; R. Nussbaum AG 55033.25 de Visibility=Nein; R. Nussbaum AG 55033.26 de Visibility=Nein; R. Nussbaum AG 55033.27 de Visibility=Nein; R. Nussbaum AG 55033.28 de Visibility=Nein; R. Nussbaum AG 55033.29 de Visibility=Nein; R. Nussbaum AG 55033.30 de Visibility=Nein; R. Nussbaum AG 55033.31 de Visibility=Nein; R. Nussbaum AG 55033.32 de Visibility=Nein; R. Nussbaum AG 55033.33 de Visibility=Nein; R. Nussbaum AG 55033.34 de Visibility=Nein; R. Nussbaum AG 55033.35 de Visibility=Nein; R. Nussbaum AG 55033.36 de Visibility=Nein; R. Nussbaum AG 55033.37 de Visibility=Nein; R. Nussbaum AG 55033.70 de Visibility=Nein; R. Nussbaum AG 55033.71 de Visibility=Nein; R. Nussbaum AG 55033.72 de Visibility=Nein; R. Nussbaum AG 55033.73 de Visibility=Nein; R. Nussbaum AG 55033.74 de Visibility=Nein

note: [stored X ft] marks values corroborated as IEEE doubles in the binary element streams (Revit-internal decimal feet)

## geometry (parser evidence)
native form markers: Sweep x3
no freeform markers — native parametric forms only
